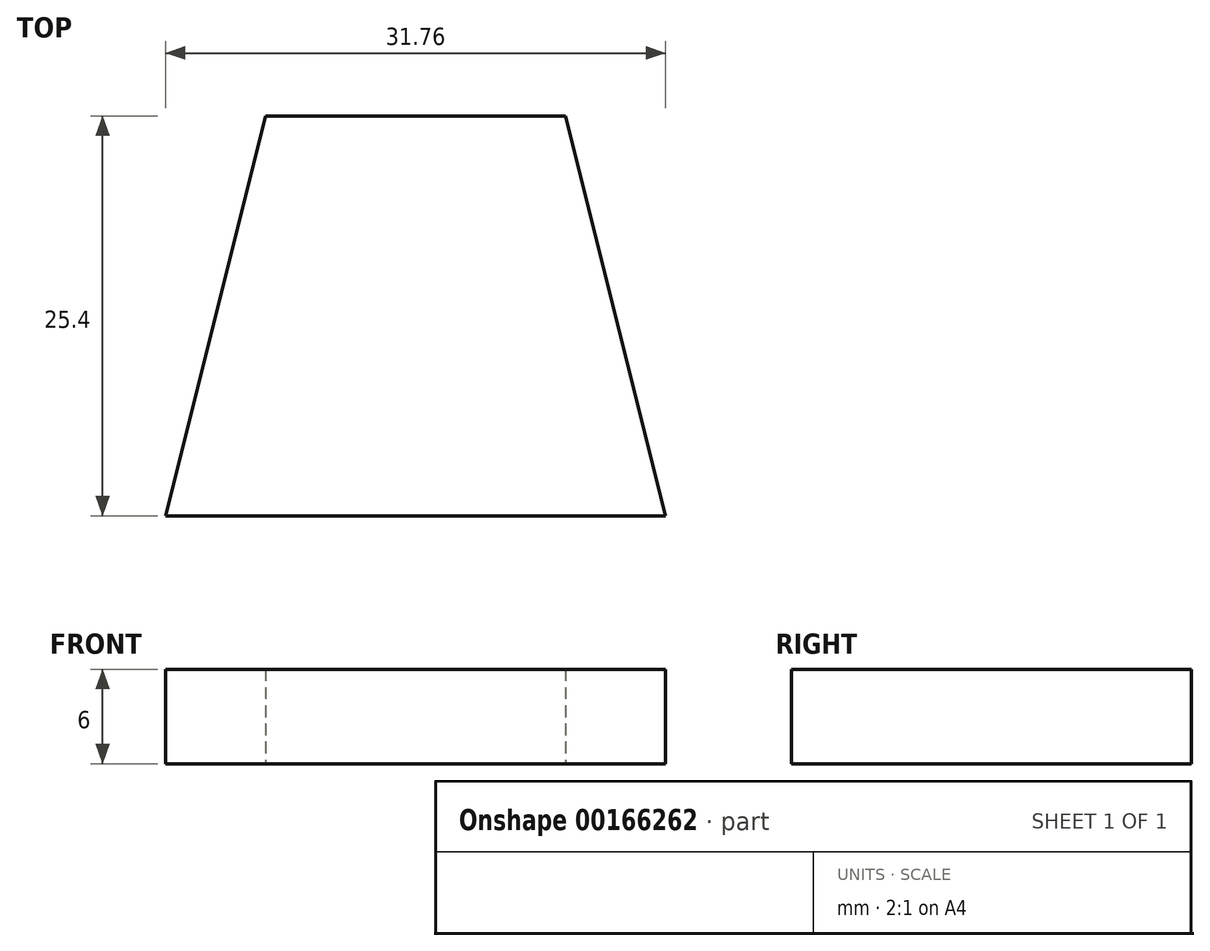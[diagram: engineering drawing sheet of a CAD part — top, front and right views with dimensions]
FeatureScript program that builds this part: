
annotation { "Feature Type Name" : "Feature", "Feature Type Description" : "" }
export const myFeature = defineFeature(function(context is Context, id is Id, definition is map)
    precondition{}
    {
        {
            var Q0;
            Q0=qCreatedBy(makeId("Top.planeOp"),FACE);
            var sketch = newSketch(context, id + "F0", { "sketchPlane" : qUnion([Q0])});
            skLineSegment(sketch, "E0", {"start": v(-15.88, -13.11) * mm, "end": v(15.88, -13.11) * mm});
            skLineSegment(sketch, "E1", {"start": v(15.88, -13.11) * mm, "end": v(9.52, 12.29) * mm});
            skLineSegment(sketch, "E2", {"start": v(9.53, 12.29) * mm, "end": v(-9.53, 12.29) * mm});
            skLineSegment(sketch, "E3", {"start": v(-9.53, 12.29) * mm, "end": v(-15.88, -13.11) * mm});
            skSolve(sketch);
        }
        {
            var Q0;
            Q0 = qSketchRegion(id + "F0", true);
            extrude(context, id + "F1", {"entities" : qUnion([Q0]), "depth" : 6 * mm});
        }
    });
